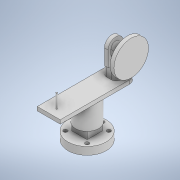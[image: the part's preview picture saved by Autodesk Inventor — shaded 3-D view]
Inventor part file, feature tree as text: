
AUTODESK INVENTOR PART (.ipt)
format: ipt  version: 2022.3 (Build 263350000, 350)  size: 255,488 bytes
history: native  units: in
note: dims shown in document units (in); Inventor stores cm internally (conversion verified against a paired STEP export)
features: extrude x12, sketch x12, fillet x2
ambient origin geometry x8: Origin, YZ Plane, XZ Plane, XY Plane, X Axis, Y Axis, Z Axis, Center Point
bodies: Solid1 (feature_tree)
feature tree (26):
  extrude  "Extrusion1"  Depth=0.7874in
  extrude  "Extrusion2"  Depth=1.1811in
  extrude  "Extrusion3"  Depth=1.1811in
  extrude  "Extrusion4"  Depth=0.1969in TaperAngle=0.0deg
  fillet  "Fillet1"  Radius=0.5118in
  extrude  "Extrusion5"  Depth=0.1181in
  extrude  "Extrusion6"  Depth=1.378in
  extrude  "Extrusion7"  Depth=0.3937in
  extrude  "Extrusion8"  Depth=0.1969in TaperAngle=0.0deg
  extrude  "Extrusion9"  Depth=0.3937in TaperAngle=0.0deg
  fillet  "Fillet2"  Radius=0.5118in
  extrude  "Extrusion10"  Depth=0.1969in
  extrude  "Extrusion11"  TaperAngle=0.0deg  [1 undecoded]
  extrude  "Extrusion13"  Depth=1.1811in TaperAngle=0.0deg
  sketch  "Sketch1"  dims[d0=0.7874in d1=0.7874in]
  sketch  "Sketch2"  dims[d2=0.7874in d3=0.0in d4=1.1811in]
  sketch  "Sketch3"  dims[d5=1.1811in d6=0.0in d7=1.1811in]
  sketch  "Sketch4"  dims[d8=3.937in d9=0.1969in d10=0.0in d11=0.5118in]
  sketch  "Sketch5"  dims[d12=0.5118in d13=0.1181in]
  sketch  "Sketch6"  dims[d14=0.1181in d15=1.378in]
  sketch  "Sketch7"  dims[d16=0.1969in d17=0.0in d18=0.3937in]
  sketch  "Sketch8"  dims[d19=0.0787in d20=0.1969in d21=0.0in]
  sketch  "Sketch9"  dims[d22=0.7874in d23=0.7874in d24=135.0deg d25=0.1969in d26=0.1969in d27=0.7874in d28=90.0deg d29=0.1969in d30=0.7874in d31=90.0deg d32=0.1969in d33=0.7874in d34=90.0deg d35=0.1969in d36=0.7874in d37=0.7874in d38=0.3937in d39=0.0in d40=0.5118in d41=0.5118in]
  sketch  "Sketch10"  dims[d42=0.5906in d43=0.1969in d44=0.0in d45=0.0in d46=0.1969in d47=0.7874in]
  sketch  "Sketch11"  dims[d48=0.5118in d49=0.5118in d50=1.378in d51=0.0in]
  sketch  "Sketch13"  dims[d52=0.0in d53=1.1811in d54=0.0in d55=0.5118in d56=0.5118in d57=0.2362in d58=0.5118in d59=1.1811in d60=0.0in d61=0.3937in d63=0.9055in d64=0.0in d65=0.5118in d66=0.5118in d67=0.2362in d68=0.5906in d69=0.0in d74=0.1969in d75=0.0in d76=1.7717in d77=0.1969in d78=0.0in]
note: 1 required parameter value undecoded (feature->parameter linkage not recoverable at this tier; creation-order binding heuristic only, values carry confidence <= 0.55)
